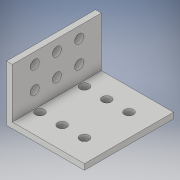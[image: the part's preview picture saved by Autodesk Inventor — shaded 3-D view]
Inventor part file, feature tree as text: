
AUTODESK INVENTOR PART (.ipt)
format: ipt  version: 2018 (Build 220112000, 112)  size: 167,424 bytes
history: native  units: in
note: dims shown in document units (in); Inventor stores cm internally (conversion verified against a paired STEP export)
features: extrude x3, sketch x3
ambient origin geometry x8: Origin, YZ Plane, XZ Plane, XY Plane, X Axis, Y Axis, Z Axis, Center Point
bodies: Solid1 (feature_tree)
feature tree (6):
  extrude  "Extrusion1"  Depth=0.13in
  extrude  "Extrusion3"  Depth=2.0in
  extrude  "Extrusion6"  Depth=1.25in
  sketch  "Sketch1"  dims[d1=0.13in d2=0.13in]
  sketch  "Sketch3"  dims[d4=2.0in d5=0.0in d9=0.5in]
  sketch  "Sketch4"  dims[d10=0.5in d11=0.5in d12=0.5in d13=0.5in d14=0.5in d15=0.5in d16=0.5in d17=0.5in d18=0.2031in d19=0.2031in d20=0.2031in d21=0.2031in d22=0.2031in d23=0.2031in d24=2.0in d25=0.0in d26=0.5in d27=0.25in d28=0.5in d29=0.5in d31=0.53in d32=0.2031in d33=0.2031in d34=0.2031in d37=0.25in d38=0.5in d39=0.5in d40=0.5in d41=0.2031in d42=0.2031in d43=0.2031in d50=1.75in d52=0.2031in d53=0.5in d54=0.2031in d55=1.0in d56=0.0in d57=1.25in]
